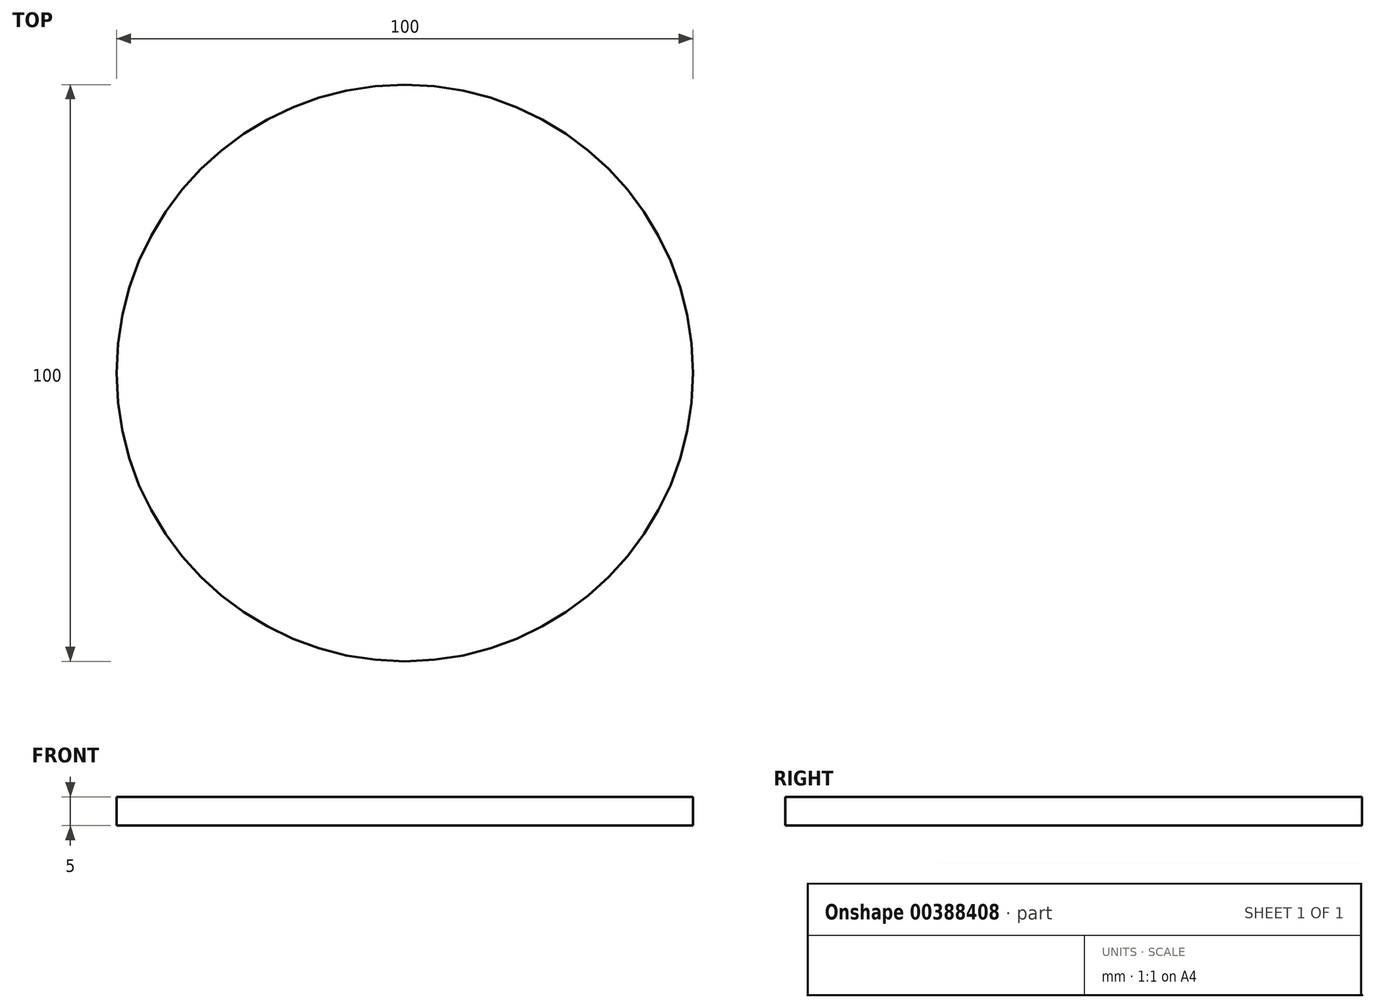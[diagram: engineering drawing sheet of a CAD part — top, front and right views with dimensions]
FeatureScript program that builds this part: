
annotation { "Feature Type Name" : "Feature", "Feature Type Description" : "" }
export const myFeature = defineFeature(function(context is Context, id is Id, definition is map)
    precondition{}
    {
        {
            var Q0;
            Q0=qCreatedBy(makeId("Top.planeOp"),FACE);
            var sketch = newSketch(context, id + "F0", { "sketchPlane" : qUnion([Q0])});
            skCircle(sketch, "E0", {"center": v(0, 0) * mm, "radius": 50 * mm});
            skSolve(sketch);
        }
        {
            var Q0;
            Q0 = qSketchRegion(id + "F0", true);
            extrude(context, id + "F1", {"entities" : qUnion([Q0]), "depth" : 5 * mm, "offsetDistance" : 25 * mm});
        }
    });
